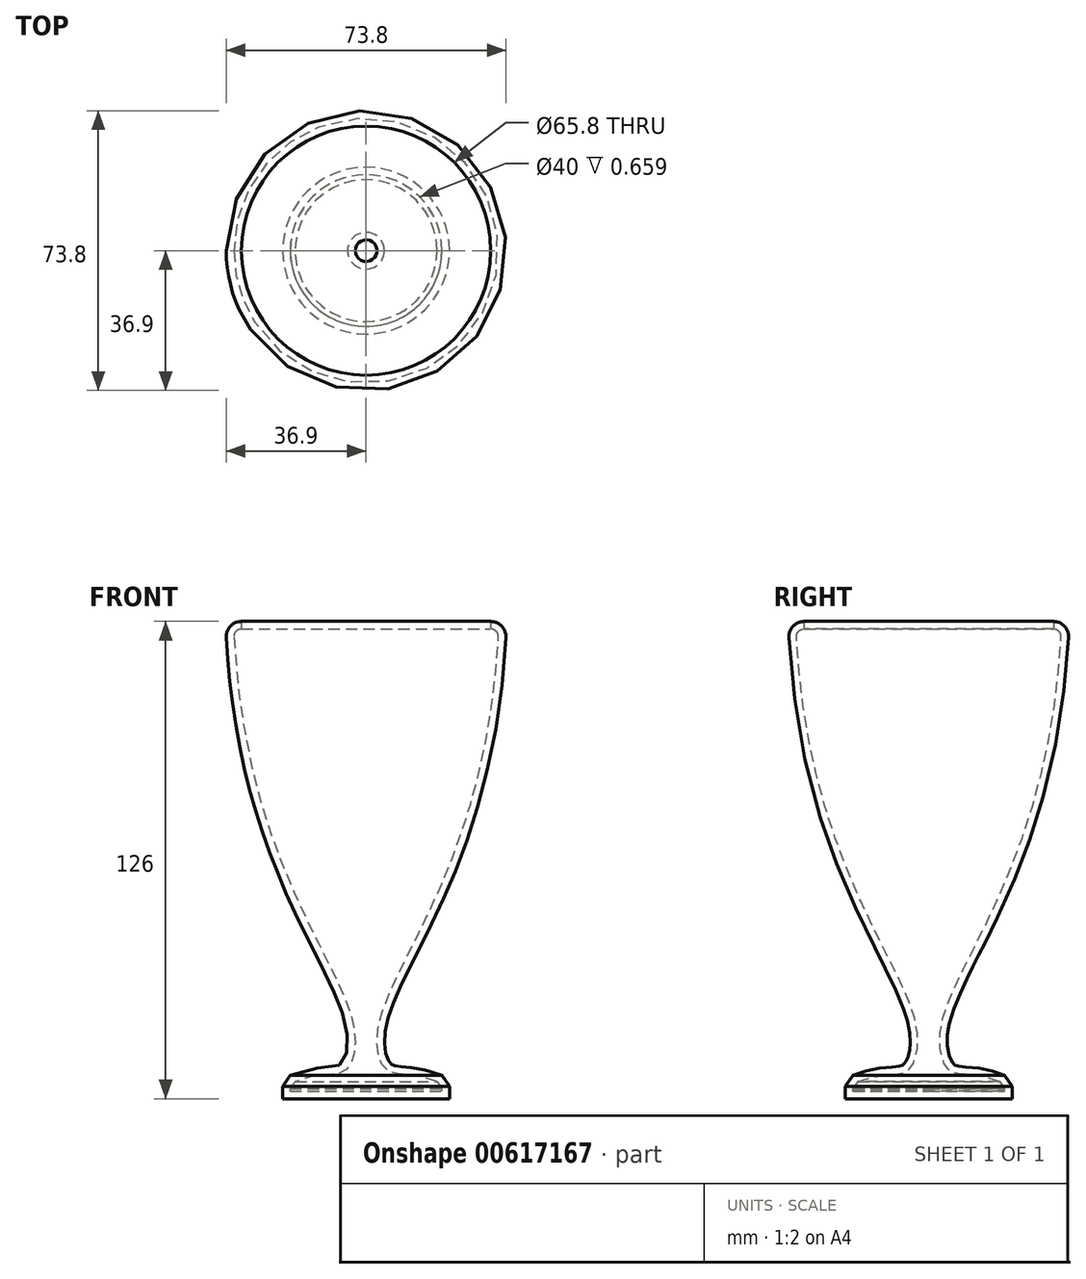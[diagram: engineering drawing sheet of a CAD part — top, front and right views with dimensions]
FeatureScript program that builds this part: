
annotation { "Feature Type Name" : "Feature", "Feature Type Description" : "" }
export const myFeature = defineFeature(function(context is Context, id is Id, definition is map)
    precondition{}
    {
        {
            var Q0;
            Q0=qCreatedBy(makeId("Front.planeOp"),FACE);
            var sketch = newSketch(context, id + "F0", { "sketchPlane" : qUnion([Q0])});
            skLineSegment(sketch, "E0", {"start": v(0, 0) * mm, "end": v(20, 0) * mm});
            skLineSegment(sketch, "E1", {"start": v(0, 0) * mm, "end": v(0, 120) * mm});
            skLineSegment(sketch, "E2", {"start": v(0, 120) * mm, "end": v(35, 120) * mm});
            skFitSpline(sketch, "E3", {"points": [v(35, 120) * mm, v(3.44, 16.07) * mm, v(5.6, 3.37) * mm, v(20, 0) * mm], "startDerivative": vector(-13.75, -308.88) * mm, "endDerivative": vector(111.7, -48.55) * mm});
            skSolve(sketch);
        }
        {
            var Q0;
            Q0=makeQuery(id+"F0.imprint","IMPRINT",FACE,{"disambiguationData":[TD([[makeQuery(id+"F0.imprint","IMPRINT",EDGE,{"derivedFrom":sQuery(id+"F0.wireOp",EDGE,"E0")}),1.0]])]});
            var Q1;
            Q1=sQuery(id+"F0.wireOp",EDGE,"E1");
            revolve(context, id + "F1", {"entities" : qUnion([Q0]), "axis" : qUnion([Q1]), "revolveType" : RevolveType.FULL});
        }
        {
            var Q0;
            Q0=makeQuery(id+"F1.opRevolve","SWEPT_FACE",FACE,{"disambiguationData":[OSD([sQuery(id+"F0.wireOp",EDGE,"E0")])]});
            extrude(context, id + "F2", {"entities" : qUnion([Q0]), "operationType" : NewBodyOperationType.ADD, "depth" : 2 * mm, "offsetDistance" : 25 * mm});
        }
        {
            var Q0;
            Q0=makeQuery(id+"F1.opRevolve","SWEPT_FACE",FACE,{"disambiguationData":[OSD([sQuery(id+"F0.wireOp",EDGE,"E2")])]});
            fillet(context, id + "F3", {"entities" : qUnion([Q0]), "radius" : 2 * mm, "tangentPropagation" : true, "allowEdgeOverflow" : false});
        }
        {
            var Q0;
            Q0=makeQuery(id+"F1.opRevolve","SWEPT_FACE",FACE,{"disambiguationData":[OSD([sQuery(id+"F0.wireOp",EDGE,"E3")])]});
            chamfer(context, id + "F4", {"entities" : qUnion([Q0]), "width" : 2 * mm, "tangentPropagation" : true});
        }
        {
            var Q0;
            Q0=makeQuery(id+"F1.opRevolve","SWEPT_FACE",FACE,{"disambiguationData":[OSD([sQuery(id+"F0.wireOp",EDGE,"E2")])]});
            shell(context, id + "F5", {"entities" : qUnion([Q0]), "thickness" : 2 * mm, "oppositeDirection" : true});
        }
    });
